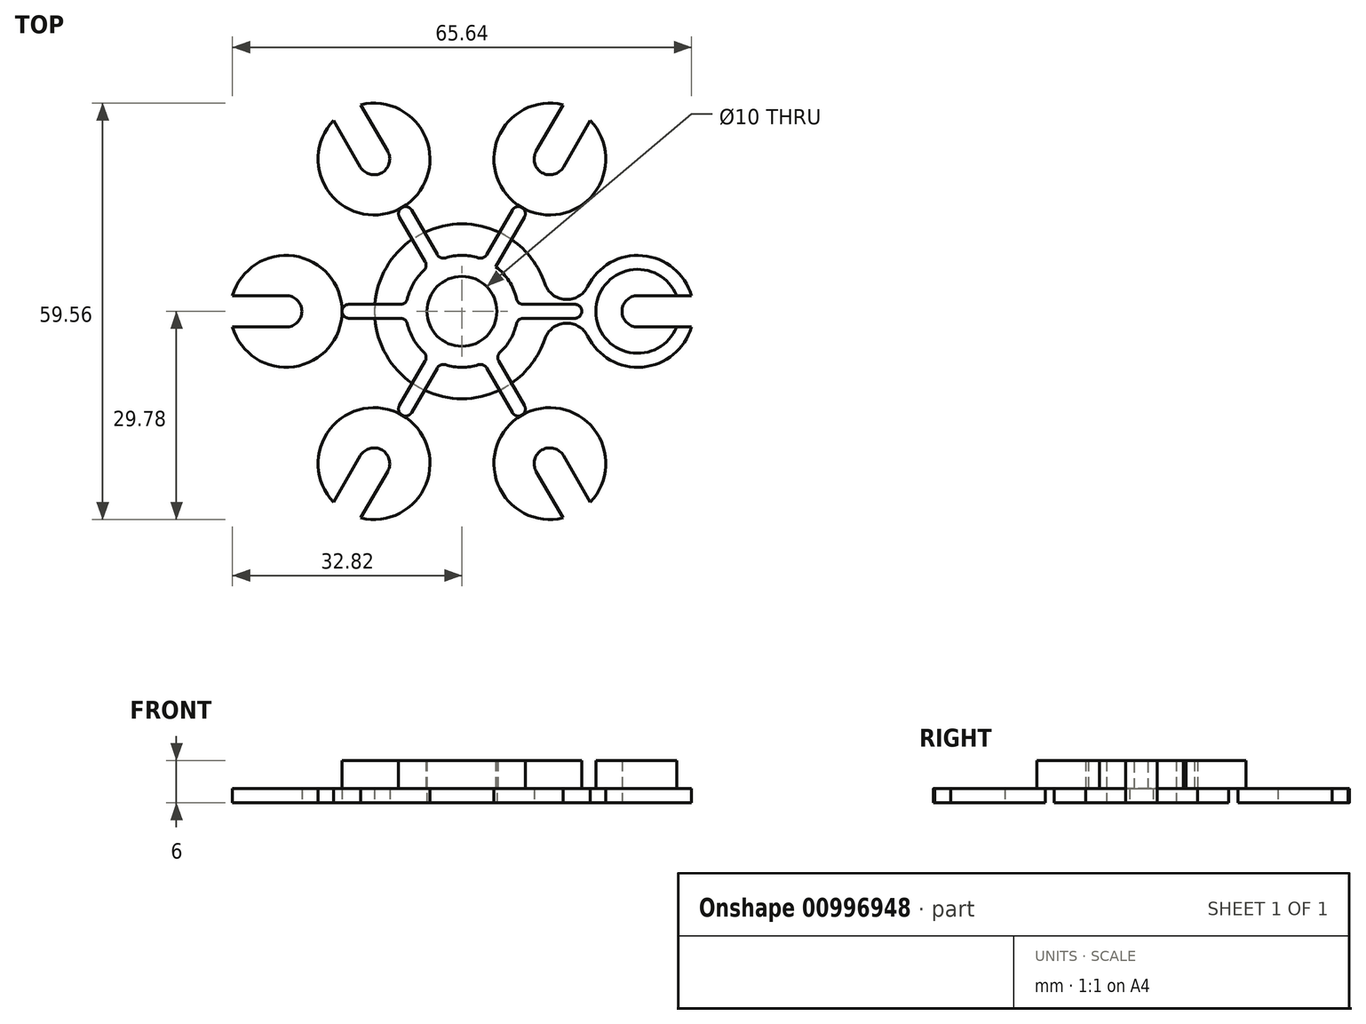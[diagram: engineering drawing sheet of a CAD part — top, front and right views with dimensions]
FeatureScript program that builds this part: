
annotation { "Feature Type Name" : "Feature", "Feature Type Description" : "" }
export const myFeature = defineFeature(function(context is Context, id is Id, definition is map)
    precondition{}
    {
        {
            var Q0;
            Q0=qCreatedBy(makeId("Top.planeOp"),FACE);
            var sketch = newSketch(context, id + "F0", { "sketchPlane" : qUnion([Q0])});
            skCircle(sketch, "E0", {"center": v(25.15, 0) * mm, "radius": 8 * mm});
            skCircle(sketch, "E1", {"center": v(0, 0) * mm, "radius": 12.5 * mm});
            skArc(sketch, "E2", {"start": v(11.86, 3.95) * mm, "mid": v(14.77, 1.7) * mm, "end": v(17.97, 3.54) * mm});
            skArc(sketch, "E3.MirrorCS", {"start": v(11.86, -3.95) * mm, "mid": v(14.77, -1.7) * mm, "end": v(17.97, -3.54) * mm});
            skCircle(sketch, "E4", {"center": v(25.15, 0) * mm, "radius": 2.25 * mm});
            skLineSegment(sketch, "E5", {"start": v(25.15, 2.25) * mm, "end": v(32.82, 2.25) * mm});
            skLineSegment(sketch, "E6.MirrorCS", {"start": v(25.15, -2.25) * mm, "end": v(32.82, -2.25) * mm});
            skCircle(sketch, "E7.1.0", {"center": v(12.57, 21.78) * mm, "radius": 2.25 * mm});
            skArc(sketch, "E7.1.1", {"start": v(9.35, 8.3) * mm, "mid": v(8.86, 11.95) * mm, "end": v(12.05, 13.8) * mm});
            skLineSegment(sketch, "E7.1.2", {"start": v(14.52, 20.65) * mm, "end": v(18.36, 27.3) * mm});
            skCircle(sketch, "E7.1.3", {"center": v(12.57, 21.78) * mm, "radius": 8 * mm});
            skLineSegment(sketch, "E7.1.4", {"start": v(10.62, 22.9) * mm, "end": v(14.46, 29.55) * mm});
            skArc(sketch, "E7.1.5", {"start": v(2.5, 12.25) * mm, "mid": v(5.92, 13.64) * mm, "end": v(5.92, 17.33) * mm});
            skCircle(sketch, "E7.2.0", {"center": v(-12.57, 21.78) * mm, "radius": 2.25 * mm});
            skArc(sketch, "E7.2.1", {"start": v(-2.5, 12.25) * mm, "mid": v(-5.92, 13.64) * mm, "end": v(-5.92, 17.33) * mm});
            skLineSegment(sketch, "E7.2.2", {"start": v(-10.62, 22.9) * mm, "end": v(-14.46, 29.55) * mm});
            skCircle(sketch, "E7.2.3", {"center": v(-12.57, 21.78) * mm, "radius": 8 * mm});
            skLineSegment(sketch, "E7.2.4", {"start": v(-14.52, 20.65) * mm, "end": v(-18.36, 27.3) * mm});
            skArc(sketch, "E7.2.5", {"start": v(-9.35, 8.3) * mm, "mid": v(-8.86, 11.95) * mm, "end": v(-12.05, 13.8) * mm});
            skCircle(sketch, "E7.3.0", {"center": v(-25.15, 0) * mm, "radius": 2.25 * mm});
            skArc(sketch, "E7.3.1", {"start": v(-11.86, 3.95) * mm, "mid": v(-14.77, 1.7) * mm, "end": v(-17.97, 3.54) * mm});
            skLineSegment(sketch, "E7.3.2", {"start": v(-25.15, 2.25) * mm, "end": v(-32.82, 2.25) * mm});
            skCircle(sketch, "E7.3.3", {"center": v(-25.15, 0) * mm, "radius": 8 * mm});
            skLineSegment(sketch, "E7.3.4", {"start": v(-25.15, -2.25) * mm, "end": v(-32.82, -2.25) * mm});
            skArc(sketch, "E7.3.5", {"start": v(-11.86, -3.95) * mm, "mid": v(-14.77, -1.7) * mm, "end": v(-17.97, -3.54) * mm});
            skCircle(sketch, "E7.4.0", {"center": v(-12.57, -21.78) * mm, "radius": 2.25 * mm});
            skArc(sketch, "E7.4.1", {"start": v(-9.35, -8.3) * mm, "mid": v(-8.86, -11.95) * mm, "end": v(-12.05, -13.8) * mm});
            skLineSegment(sketch, "E7.4.2", {"start": v(-14.52, -20.65) * mm, "end": v(-18.36, -27.3) * mm});
            skCircle(sketch, "E7.4.3", {"center": v(-12.57, -21.78) * mm, "radius": 8 * mm});
            skLineSegment(sketch, "E7.4.4", {"start": v(-10.62, -22.9) * mm, "end": v(-14.46, -29.55) * mm});
            skArc(sketch, "E7.4.5", {"start": v(-2.5, -12.25) * mm, "mid": v(-5.92, -13.64) * mm, "end": v(-5.92, -17.33) * mm});
            skCircle(sketch, "E7.5.0", {"center": v(12.57, -21.78) * mm, "radius": 2.25 * mm});
            skArc(sketch, "E7.5.1", {"start": v(2.5, -12.25) * mm, "mid": v(5.92, -13.64) * mm, "end": v(5.92, -17.33) * mm});
            skLineSegment(sketch, "E7.5.2", {"start": v(10.62, -22.9) * mm, "end": v(14.46, -29.55) * mm});
            skCircle(sketch, "E7.5.3", {"center": v(12.57, -21.78) * mm, "radius": 8 * mm});
            skLineSegment(sketch, "E7.5.4", {"start": v(14.52, -20.65) * mm, "end": v(18.36, -27.3) * mm});
            skArc(sketch, "E7.5.5", {"start": v(9.35, -8.3) * mm, "mid": v(8.86, -11.95) * mm, "end": v(12.05, -13.8) * mm});
            skCircle(sketch, "E8", {"center": v(0, 0) * mm, "radius": 5 * mm});
            skSolve(sketch);
        }
        {
            var Q0;
            {var subQ0=sQuery(id+"F0.wireOp",EDGE,"E5");Q0=makeQuery(id+"F0.imprint","IMPRINT",FACE,{"disambiguationData":[TD([[makeQuery(id+"F0.imprint","IMPRINT",EDGE,{"derivedFrom":subQ0}),1.0]])]});}
            var Q1;
            {var subQ0=sQuery(id+"F0.wireOp",EDGE,"E2");Q1=makeQuery(id+"F0.imprint","IMPRINT",FACE,{"disambiguationData":[TD([[makeQuery(id+"F0.imprint","IMPRINT",EDGE,{"derivedFrom":subQ0}),-1.0]])]});}
            var Q2;
            {var subQ0=sQuery(id+"F0.wireOp",EDGE,"E1");var subQ8=makeQuery(id+"F0.imprint","INTERSECT",VERTEX,{"derivedFrom":[subQ0,sQuery(id+"F0.wireOp",EDGE,"E2")]});Q2=makeQuery(id+"F0.imprint","IMPRINT",FACE,{"disambiguationData":[TD([[makeQuery(id+"F0.imprint","IMPRINT",EDGE,{"disambiguationData":[TD([[subQ8,-1.0]])],"derivedFrom":subQ0}),1.0]])]});}
            var Q3;
            {var subQ0=sQuery(id+"F0.wireOp",EDGE,"19b5fdfa-99aa-4df6-ab24-c400294d4a82.1.0");Q3=makeQuery(id+"F0.imprint","IMPRINT",FACE,{"disambiguationData":[TD([[makeQuery(id+"F0.imprint","IMPRINT",EDGE,{"derivedFrom":subQ0}),1.0]])]});}
            var Q4;
            {var subQ0=sQuery(id+"F0.wireOp",EDGE,"20f51366-0cb7-4326-9ac2-2f9416bb62c2.1.0");Q4=makeQuery(id+"F0.imprint","IMPRINT",FACE,{"disambiguationData":[TD([[makeQuery(id+"F0.imprint","IMPRINT",EDGE,{"derivedFrom":subQ0}),-1.0]])]});}
            var Q5;
            {var subQ0=sQuery(id+"F0.wireOp",EDGE,"20f51366-0cb7-4326-9ac2-2f9416bb62c2.2.0");Q5=makeQuery(id+"F0.imprint","IMPRINT",FACE,{"disambiguationData":[TD([[makeQuery(id+"F0.imprint","IMPRINT",EDGE,{"derivedFrom":subQ0}),-1.0]])]});}
            var Q6;
            {var subQ4=sQuery(id+"F0.wireOp",EDGE,"19b5fdfa-99aa-4df6-ab24-c400294d4a82.2.0");Q6=makeQuery(id+"F0.imprint","IMPRINT",FACE,{"disambiguationData":[TD([[makeQuery(id+"F0.imprint","IMPRINT",EDGE,{"derivedFrom":subQ4}),1.0]])]});}
            var Q7;
            {var subQ0=sQuery(id+"F0.wireOp",EDGE,"19b5fdfa-99aa-4df6-ab24-c400294d4a82.3.0");Q7=makeQuery(id+"F0.imprint","IMPRINT",FACE,{"disambiguationData":[TD([[makeQuery(id+"F0.imprint","IMPRINT",EDGE,{"derivedFrom":subQ0}),1.0]])]});}
            var Q8;
            {var subQ0=sQuery(id+"F0.wireOp",EDGE,"20f51366-0cb7-4326-9ac2-2f9416bb62c2.3.0");Q8=makeQuery(id+"F0.imprint","IMPRINT",FACE,{"disambiguationData":[TD([[makeQuery(id+"F0.imprint","IMPRINT",EDGE,{"derivedFrom":subQ0}),-1.0]])]});}
            var Q9;
            {var subQ0=sQuery(id+"F0.wireOp",EDGE,"20f51366-0cb7-4326-9ac2-2f9416bb62c2.4.0");Q9=makeQuery(id+"F0.imprint","IMPRINT",FACE,{"disambiguationData":[TD([[makeQuery(id+"F0.imprint","IMPRINT",EDGE,{"derivedFrom":subQ0}),-1.0]])]});}
            var Q10;
            {var subQ3=sQuery(id+"F0.wireOp",EDGE,"19b5fdfa-99aa-4df6-ab24-c400294d4a82.4.0");Q10=makeQuery(id+"F0.imprint","IMPRINT",FACE,{"disambiguationData":[TD([[makeQuery(id+"F0.imprint","IMPRINT",EDGE,{"derivedFrom":subQ3}),1.0]])]});}
            var Q11;
            {var subQ0=sQuery(id+"F0.wireOp",EDGE,"20f51366-0cb7-4326-9ac2-2f9416bb62c2.5.0");Q11=makeQuery(id+"F0.imprint","IMPRINT",FACE,{"disambiguationData":[TD([[makeQuery(id+"F0.imprint","IMPRINT",EDGE,{"derivedFrom":subQ0}),-1.0]])]});}
            var Q12;
            {var subQ0=sQuery(id+"F0.wireOp",EDGE,"19b5fdfa-99aa-4df6-ab24-c400294d4a82.5.0");Q12=makeQuery(id+"F0.imprint","IMPRINT",FACE,{"disambiguationData":[TD([[makeQuery(id+"F0.imprint","IMPRINT",EDGE,{"derivedFrom":subQ0}),1.0]])]});}
            var Q13;
            {var subQ0=sQuery(id+"F0.wireOp",EDGE,"E7.1.1");Q13=makeQuery(id+"F0.imprint","IMPRINT",FACE,{"disambiguationData":[TD([[makeQuery(id+"F0.imprint","IMPRINT",EDGE,{"derivedFrom":subQ0}),1.0]])]});}
            var Q14;
            {var subQ0=sQuery(id+"F0.wireOp",EDGE,"E7.2.1");Q14=makeQuery(id+"F0.imprint","IMPRINT",FACE,{"disambiguationData":[TD([[makeQuery(id+"F0.imprint","IMPRINT",EDGE,{"derivedFrom":subQ0}),1.0]])]});}
            var Q15;
            {var subQ0=sQuery(id+"F0.wireOp",EDGE,"E7.3.1");Q15=makeQuery(id+"F0.imprint","IMPRINT",FACE,{"disambiguationData":[TD([[makeQuery(id+"F0.imprint","IMPRINT",EDGE,{"derivedFrom":subQ0}),1.0]])]});}
            var Q16;
            {var subQ0=sQuery(id+"F0.wireOp",EDGE,"E7.4.1");Q16=makeQuery(id+"F0.imprint","IMPRINT",FACE,{"disambiguationData":[TD([[makeQuery(id+"F0.imprint","IMPRINT",EDGE,{"derivedFrom":subQ0}),1.0]])]});}
            var Q17;
            {var subQ0=sQuery(id+"F0.wireOp",EDGE,"E7.5.1");Q17=makeQuery(id+"F0.imprint","IMPRINT",FACE,{"disambiguationData":[TD([[makeQuery(id+"F0.imprint","IMPRINT",EDGE,{"derivedFrom":subQ0}),1.0]])]});}
            var Q18;
            {var subQ3=sQuery(id+"F0.wireOp",EDGE,"E7.5.2");Q18=makeQuery(id+"F0.imprint","IMPRINT",FACE,{"disambiguationData":[TD([[makeQuery(id+"F0.imprint","IMPRINT",EDGE,{"derivedFrom":subQ3}),-1.0]])]});}
            var Q19;
            {var subQ3=sQuery(id+"F0.wireOp",EDGE,"E7.4.2");Q19=makeQuery(id+"F0.imprint","IMPRINT",FACE,{"disambiguationData":[TD([[makeQuery(id+"F0.imprint","IMPRINT",EDGE,{"derivedFrom":subQ3}),-1.0]])]});}
            var Q20;
            {var subQ3=sQuery(id+"F0.wireOp",EDGE,"E7.3.2");Q20=makeQuery(id+"F0.imprint","IMPRINT",FACE,{"disambiguationData":[TD([[makeQuery(id+"F0.imprint","IMPRINT",EDGE,{"derivedFrom":subQ3}),-1.0]])]});}
            var Q21;
            {var subQ3=sQuery(id+"F0.wireOp",EDGE,"E7.2.2");Q21=makeQuery(id+"F0.imprint","IMPRINT",FACE,{"disambiguationData":[TD([[makeQuery(id+"F0.imprint","IMPRINT",EDGE,{"derivedFrom":subQ3}),-1.0]])]});}
            var Q22;
            {var subQ3=sQuery(id+"F0.wireOp",EDGE,"E7.1.2");Q22=makeQuery(id+"F0.imprint","IMPRINT",FACE,{"disambiguationData":[TD([[makeQuery(id+"F0.imprint","IMPRINT",EDGE,{"derivedFrom":subQ3}),-1.0]])]});}
            extrude(context, id + "F1", {"entities" : qUnion([Q0, Q1, Q2, Q3, Q4, Q5, Q6, Q7, Q8, Q9, Q10, Q11, Q12, Q13, Q14, Q15, Q16, Q17, Q18, Q19, Q20, Q21, Q22]), "depth" : 2 * mm, "offsetDistance" : 25 * mm});
        }
        {
            var Q0;
            Q0=makeQuery(id+"F1.opExtrude","CAP_FACE",FACE,{"disambiguationData":[OSD([sQuery(id+"F0.wireOp",EDGE,"E0"),sQuery(id+"F0.wireOp",EDGE,"E1"),sQuery(id+"F0.wireOp",EDGE,"E2"),sQuery(id+"F0.wireOp",EDGE,"E3.MirrorCS"),sQuery(id+"F0.wireOp",EDGE,"20f51366-0cb7-4326-9ac2-2f9416bb62c2.1.0"),sQuery(id+"F0.wireOp",EDGE,"20f51366-0cb7-4326-9ac2-2f9416bb62c2.1.1"),sQuery(id+"F0.wireOp",EDGE,"20f51366-0cb7-4326-9ac2-2f9416bb62c2.1.2"),sQuery(id+"F0.wireOp",EDGE,"20f51366-0cb7-4326-9ac2-2f9416bb62c2.2.0"),sQuery(id+"F0.wireOp",EDGE,"20f51366-0cb7-4326-9ac2-2f9416bb62c2.2.1"),sQuery(id+"F0.wireOp",EDGE,"20f51366-0cb7-4326-9ac2-2f9416bb62c2.2.2"),sQuery(id+"F0.wireOp",EDGE,"20f51366-0cb7-4326-9ac2-2f9416bb62c2.3.0"),sQuery(id+"F0.wireOp",EDGE,"20f51366-0cb7-4326-9ac2-2f9416bb62c2.3.1"),sQuery(id+"F0.wireOp",EDGE,"20f51366-0cb7-4326-9ac2-2f9416bb62c2.3.2"),sQuery(id+"F0.wireOp",EDGE,"20f51366-0cb7-4326-9ac2-2f9416bb62c2.4.0"),sQuery(id+"F0.wireOp",EDGE,"20f51366-0cb7-4326-9ac2-2f9416bb62c2.4.1"),sQuery(id+"F0.wireOp",EDGE,"20f51366-0cb7-4326-9ac2-2f9416bb62c2.4.2"),sQuery(id+"F0.wireOp",EDGE,"20f51366-0cb7-4326-9ac2-2f9416bb62c2.5.0"),sQuery(id+"F0.wireOp",EDGE,"20f51366-0cb7-4326-9ac2-2f9416bb62c2.5.1"),sQuery(id+"F0.wireOp",EDGE,"20f51366-0cb7-4326-9ac2-2f9416bb62c2.5.2"),sQuery(id+"F0.wireOp",EDGE,"E4"),sQuery(id+"F0.wireOp",EDGE,"E5"),sQuery(id+"F0.wireOp",EDGE,"E6.MirrorCS"),sQuery(id+"F0.wireOp",EDGE,"19b5fdfa-99aa-4df6-ab24-c400294d4a82.1.0"),sQuery(id+"F0.wireOp",EDGE,"19b5fdfa-99aa-4df6-ab24-c400294d4a82.1.1"),sQuery(id+"F0.wireOp",EDGE,"19b5fdfa-99aa-4df6-ab24-c400294d4a82.1.2"),sQuery(id+"F0.wireOp",EDGE,"19b5fdfa-99aa-4df6-ab24-c400294d4a82.2.0"),sQuery(id+"F0.wireOp",EDGE,"19b5fdfa-99aa-4df6-ab24-c400294d4a82.2.1"),sQuery(id+"F0.wireOp",EDGE,"19b5fdfa-99aa-4df6-ab24-c400294d4a82.2.2"),sQuery(id+"F0.wireOp",EDGE,"19b5fdfa-99aa-4df6-ab24-c400294d4a82.3.0"),sQuery(id+"F0.wireOp",EDGE,"19b5fdfa-99aa-4df6-ab24-c400294d4a82.3.1"),sQuery(id+"F0.wireOp",EDGE,"19b5fdfa-99aa-4df6-ab24-c400294d4a82.3.2"),sQuery(id+"F0.wireOp",EDGE,"19b5fdfa-99aa-4df6-ab24-c400294d4a82.4.0"),sQuery(id+"F0.wireOp",EDGE,"19b5fdfa-99aa-4df6-ab24-c400294d4a82.4.1"),sQuery(id+"F0.wireOp",EDGE,"19b5fdfa-99aa-4df6-ab24-c400294d4a82.4.2"),sQuery(id+"F0.wireOp",EDGE,"19b5fdfa-99aa-4df6-ab24-c400294d4a82.5.0"),sQuery(id+"F0.wireOp",EDGE,"19b5fdfa-99aa-4df6-ab24-c400294d4a82.5.1"),sQuery(id+"F0.wireOp",EDGE,"19b5fdfa-99aa-4df6-ab24-c400294d4a82.5.2"),sQuery(id+"F0.wireOp",EDGE,"Dy7Ucuv2-wQet-6OGx-sShq-DWIG0Ccbs11O")])],"isStart":false});
            var sketch = newSketch(context, id + "F2", { "sketchPlane" : qUnion([Q0])});
            skArc(sketch, "E9", {"start": v(32.82, -2.25) * mm, "mid": v(17.15, 0) * mm, "end": v(32.82, 2.25) * mm});
            skArc(sketch, "E10", {"start": v(30.7, -2.25) * mm, "mid": v(19.15, 0) * mm, "end": v(30.7, 2.25) * mm});
            skCircle(sketch, "E11", {"center": v(0, 0) * mm, "radius": 8 * mm});
            skLineSegment(sketch, "E12", {"start": v(17.2, 1) * mm, "end": v(7.94, 1) * mm});
            skLineSegment(sketch, "E13.MirrorCS", {"start": v(17.2, -1) * mm, "end": v(7.94, -1) * mm});
            skLineSegment(sketch, "E14.1.0", {"start": v(7.74, 15.4) * mm, "end": v(3.1, 7.37) * mm});
            skLineSegment(sketch, "E14.1.1", {"start": v(9.47, 14.4) * mm, "end": v(4.83, 6.37) * mm});
            skArc(sketch, "E14.1.2", {"start": v(18.36, 27.3) * mm, "mid": v(8.57, 14.85) * mm, "end": v(14.46, 29.55) * mm});
            skArc(sketch, "E14.1.3", {"start": v(17.3, 25.47) * mm, "mid": v(9.57, 16.58) * mm, "end": v(13.4, 27.72) * mm});
            skLineSegment(sketch, "E14.2.0", {"start": v(-9.47, 14.4) * mm, "end": v(-4.83, 6.37) * mm});
            skLineSegment(sketch, "E14.2.1", {"start": v(-7.74, 15.4) * mm, "end": v(-3.1, 7.37) * mm});
            skArc(sketch, "E14.2.2", {"start": v(-14.46, 29.55) * mm, "mid": v(-8.57, 14.85) * mm, "end": v(-18.36, 27.3) * mm});
            skArc(sketch, "E14.2.3", {"start": v(-13.4, 27.72) * mm, "mid": v(-9.57, 16.58) * mm, "end": v(-17.3, 25.47) * mm});
            skLineSegment(sketch, "E14.3.0", {"start": v(-17.2, -1) * mm, "end": v(-7.94, -1) * mm});
            skLineSegment(sketch, "E14.3.1", {"start": v(-17.2, 1) * mm, "end": v(-7.94, 1) * mm});
            skArc(sketch, "E14.3.2", {"start": v(-32.82, 2.25) * mm, "mid": v(-17.15, 0) * mm, "end": v(-32.82, -2.25) * mm});
            skArc(sketch, "E14.3.3", {"start": v(-30.7, 2.25) * mm, "mid": v(-19.15, 0) * mm, "end": v(-30.7, -2.25) * mm});
            skLineSegment(sketch, "E14.4.0", {"start": v(-7.74, -15.4) * mm, "end": v(-3.1, -7.37) * mm});
            skLineSegment(sketch, "E14.4.1", {"start": v(-9.47, -14.4) * mm, "end": v(-4.83, -6.37) * mm});
            skArc(sketch, "E14.4.2", {"start": v(-18.36, -27.3) * mm, "mid": v(-8.57, -14.85) * mm, "end": v(-14.46, -29.55) * mm});
            skArc(sketch, "E14.4.3", {"start": v(-17.3, -25.47) * mm, "mid": v(-9.57, -16.58) * mm, "end": v(-13.4, -27.72) * mm});
            skLineSegment(sketch, "E14.5.0", {"start": v(9.47, -14.4) * mm, "end": v(4.83, -6.37) * mm});
            skLineSegment(sketch, "E14.5.1", {"start": v(7.74, -15.4) * mm, "end": v(3.1, -7.37) * mm});
            skArc(sketch, "E14.5.2", {"start": v(14.46, -29.55) * mm, "mid": v(8.57, -14.85) * mm, "end": v(18.36, -27.3) * mm});
            skArc(sketch, "E14.5.3", {"start": v(13.4, -27.72) * mm, "mid": v(9.57, -16.58) * mm, "end": v(17.3, -25.47) * mm});
            skSolve(sketch);
        }
        {
            var Q0;
            {var subQ0=sQuery(id+"F2.wireOp",EDGE,"E12");Q0=makeQuery(id+"F2.imprint","IMPRINT",FACE,{"disambiguationData":[TD([[makeQuery(id+"F2.imprint","IMPRINT",EDGE,{"derivedFrom":subQ0}),1.0]])]});}
            var Q1;
            {var subQ9=sQuery(id+"F2.wireOp",EDGE,"E10");Q1=makeQuery(id+"F2.imprint","IMPRINT",FACE,{"disambiguationData":[TD([[makeQuery(id+"F2.imprint","IMPRINT",EDGE,{"derivedFrom":subQ9}),1.0]])]});}
            var Q2;
            Q2=makeQuery(id+"F2.imprint","IMPRINT",FACE,{"disambiguationData":[TD([[makeQuery(id+"F2.imprint","IMPRINT",EDGE,{"derivedFrom":makeQuery(id+"F1.opExtrude","CAP_EDGE",EDGE,{"disambiguationData":[OSD([sQuery(id+"F0.wireOp",EDGE,"E8")])],"isStart":false})}),-1.0]])]});
            var Q3;
            {var subQ0=sQuery(id+"F2.wireOp",EDGE,"E14.5.0");Q3=makeQuery(id+"F2.imprint","IMPRINT",FACE,{"disambiguationData":[TD([[makeQuery(id+"F2.imprint","IMPRINT",EDGE,{"derivedFrom":subQ0}),1.0]])]});}
            var Q4;
            {var subQ9=sQuery(id+"F2.wireOp",EDGE,"E14.5.3");Q4=makeQuery(id+"F2.imprint","IMPRINT",FACE,{"disambiguationData":[TD([[makeQuery(id+"F2.imprint","IMPRINT",EDGE,{"derivedFrom":subQ9}),1.0]])]});}
            var Q5;
            {var subQ5=sQuery(id+"F2.wireOp",EDGE,"E14.4.3");Q5=makeQuery(id+"F2.imprint","IMPRINT",FACE,{"disambiguationData":[TD([[makeQuery(id+"F2.imprint","IMPRINT",EDGE,{"derivedFrom":subQ5}),1.0]])]});}
            var Q6;
            {var subQ0=sQuery(id+"F2.wireOp",EDGE,"E14.4.0");Q6=makeQuery(id+"F2.imprint","IMPRINT",FACE,{"disambiguationData":[TD([[makeQuery(id+"F2.imprint","IMPRINT",EDGE,{"derivedFrom":subQ0}),1.0]])]});}
            var Q7;
            {var subQ0=sQuery(id+"F2.wireOp",EDGE,"E14.3.0");Q7=makeQuery(id+"F2.imprint","IMPRINT",FACE,{"disambiguationData":[TD([[makeQuery(id+"F2.imprint","IMPRINT",EDGE,{"derivedFrom":subQ0}),1.0]])]});}
            var Q8;
            {var subQ9=sQuery(id+"F2.wireOp",EDGE,"E14.3.3");Q8=makeQuery(id+"F2.imprint","IMPRINT",FACE,{"disambiguationData":[TD([[makeQuery(id+"F2.imprint","IMPRINT",EDGE,{"derivedFrom":subQ9}),1.0]])]});}
            var Q9;
            {var subQ7=sQuery(id+"F2.wireOp",EDGE,"E14.2.3");Q9=makeQuery(id+"F2.imprint","IMPRINT",FACE,{"disambiguationData":[TD([[makeQuery(id+"F2.imprint","IMPRINT",EDGE,{"derivedFrom":subQ7}),1.0]])]});}
            var Q10;
            {var subQ0=sQuery(id+"F2.wireOp",EDGE,"E14.2.0");Q10=makeQuery(id+"F2.imprint","IMPRINT",FACE,{"disambiguationData":[TD([[makeQuery(id+"F2.imprint","IMPRINT",EDGE,{"derivedFrom":subQ0}),1.0]])]});}
            var Q11;
            {var subQ0=sQuery(id+"F2.wireOp",EDGE,"E14.1.0");Q11=makeQuery(id+"F2.imprint","IMPRINT",FACE,{"disambiguationData":[TD([[makeQuery(id+"F2.imprint","IMPRINT",EDGE,{"derivedFrom":subQ0}),1.0]])]});}
            var Q12;
            {var subQ6=sQuery(id+"F2.wireOp",EDGE,"E14.1.3");Q12=makeQuery(id+"F2.imprint","IMPRINT",FACE,{"disambiguationData":[TD([[makeQuery(id+"F2.imprint","IMPRINT",EDGE,{"derivedFrom":subQ6}),1.0]])]});}
            extrude(context, id + "F3", {"entities" : qUnion([Q0, Q1, Q2, Q3, Q4, Q5, Q6, Q7, Q8, Q9, Q10, Q11, Q12]), "operationType" : NewBodyOperationType.ADD, "depth" : 4 * mm, "offsetDistance" : 25 * mm});
        }
        {
            var Q0;
            {var subQ0=sQuery(id+"F0.wireOp",EDGE,"E5");Q0=makeQuery(id+"F3.boolean.opBoolean","MERGE",EDGE,{"derivedFrom":[makeQuery(id+"F1.opExtrude","SWEPT_EDGE",EDGE,{"disambiguationData":[OSD([sQuery(id+"F0.wireOp",EDGE,"E0"),subQ0])]}),makeQuery(id+"F3.opExtrude","SWEPT_EDGE",EDGE,{"disambiguationData":[OSD([subQ0,sQuery(id+"F2.wireOp",EDGE,"E9")])]})]});}
            var Q1;
            {var subQ0=sQuery(id+"F0.wireOp",EDGE,"E6.MirrorCS");Q1=makeQuery(id+"F3.boolean.opBoolean","MERGE",EDGE,{"derivedFrom":[makeQuery(id+"F1.opExtrude","SWEPT_EDGE",EDGE,{"disambiguationData":[OSD([sQuery(id+"F0.wireOp",EDGE,"E0"),subQ0])]}),makeQuery(id+"F3.opExtrude","SWEPT_EDGE",EDGE,{"disambiguationData":[OSD([subQ0,sQuery(id+"F2.wireOp",EDGE,"E9")])]})]});}
            var Q2;
            {var subQ0=sQuery(id+"F0.wireOp",EDGE,"E7.1.4");Q2=makeQuery(id+"F3.boolean.opBoolean","MERGE",EDGE,{"derivedFrom":[makeQuery(id+"F1.opExtrude","SWEPT_EDGE",EDGE,{"disambiguationData":[OSD([sQuery(id+"F0.wireOp",EDGE,"E7.1.3"),subQ0])]}),makeQuery(id+"F3.opExtrude","SWEPT_EDGE",EDGE,{"disambiguationData":[OSD([subQ0,sQuery(id+"F2.wireOp",EDGE,"E14.1.2")])]})]});}
            var Q3;
            {var subQ0=sQuery(id+"F0.wireOp",EDGE,"E7.2.4");Q3=makeQuery(id+"F3.boolean.opBoolean","MERGE",EDGE,{"derivedFrom":[makeQuery(id+"F1.opExtrude","SWEPT_EDGE",EDGE,{"disambiguationData":[OSD([sQuery(id+"F0.wireOp",EDGE,"E7.2.3"),subQ0])]}),makeQuery(id+"F3.opExtrude","SWEPT_EDGE",EDGE,{"disambiguationData":[OSD([subQ0,sQuery(id+"F2.wireOp",EDGE,"E14.2.2")])]})]});}
            var Q4;
            {var subQ0=sQuery(id+"F0.wireOp",EDGE,"E7.1.2");Q4=makeQuery(id+"F3.boolean.opBoolean","MERGE",EDGE,{"derivedFrom":[makeQuery(id+"F1.opExtrude","SWEPT_EDGE",EDGE,{"disambiguationData":[OSD([subQ0,sQuery(id+"F0.wireOp",EDGE,"E7.1.3")])]}),makeQuery(id+"F3.opExtrude","SWEPT_EDGE",EDGE,{"disambiguationData":[OSD([subQ0,sQuery(id+"F2.wireOp",EDGE,"E14.1.2")])]})]});}
            var Q5;
            {var subQ0=sQuery(id+"F0.wireOp",EDGE,"E7.2.2");Q5=makeQuery(id+"F3.boolean.opBoolean","MERGE",EDGE,{"derivedFrom":[makeQuery(id+"F1.opExtrude","SWEPT_EDGE",EDGE,{"disambiguationData":[OSD([subQ0,sQuery(id+"F0.wireOp",EDGE,"E7.2.3")])]}),makeQuery(id+"F3.opExtrude","SWEPT_EDGE",EDGE,{"disambiguationData":[OSD([subQ0,sQuery(id+"F2.wireOp",EDGE,"E14.2.2")])]})]});}
            var Q6;
            {var subQ0=sQuery(id+"F0.wireOp",EDGE,"E7.3.2");Q6=makeQuery(id+"F3.boolean.opBoolean","MERGE",EDGE,{"derivedFrom":[makeQuery(id+"F1.opExtrude","SWEPT_EDGE",EDGE,{"disambiguationData":[OSD([subQ0,sQuery(id+"F0.wireOp",EDGE,"E7.3.3")])]}),makeQuery(id+"F3.opExtrude","SWEPT_EDGE",EDGE,{"disambiguationData":[OSD([subQ0,sQuery(id+"F2.wireOp",EDGE,"E14.3.2")])]})]});}
            var Q7;
            {var subQ0=sQuery(id+"F0.wireOp",EDGE,"E7.3.4");Q7=makeQuery(id+"F3.boolean.opBoolean","MERGE",EDGE,{"derivedFrom":[makeQuery(id+"F1.opExtrude","SWEPT_EDGE",EDGE,{"disambiguationData":[OSD([sQuery(id+"F0.wireOp",EDGE,"E7.3.3"),subQ0])]}),makeQuery(id+"F3.opExtrude","SWEPT_EDGE",EDGE,{"disambiguationData":[OSD([subQ0,sQuery(id+"F2.wireOp",EDGE,"E14.3.2")])]})]});}
            var Q8;
            {var subQ0=sQuery(id+"F0.wireOp",EDGE,"E7.4.2");Q8=makeQuery(id+"F3.boolean.opBoolean","MERGE",EDGE,{"derivedFrom":[makeQuery(id+"F1.opExtrude","SWEPT_EDGE",EDGE,{"disambiguationData":[OSD([subQ0,sQuery(id+"F0.wireOp",EDGE,"E7.4.3")])]}),makeQuery(id+"F3.opExtrude","SWEPT_EDGE",EDGE,{"disambiguationData":[OSD([subQ0,sQuery(id+"F2.wireOp",EDGE,"E14.4.2")])]})]});}
            var Q9;
            {var subQ0=sQuery(id+"F0.wireOp",EDGE,"E7.4.4");Q9=makeQuery(id+"F3.boolean.opBoolean","MERGE",EDGE,{"derivedFrom":[makeQuery(id+"F1.opExtrude","SWEPT_EDGE",EDGE,{"disambiguationData":[OSD([sQuery(id+"F0.wireOp",EDGE,"E7.4.3"),subQ0])]}),makeQuery(id+"F3.opExtrude","SWEPT_EDGE",EDGE,{"disambiguationData":[OSD([subQ0,sQuery(id+"F2.wireOp",EDGE,"E14.4.2")])]})]});}
            var Q10;
            {var subQ0=sQuery(id+"F0.wireOp",EDGE,"E7.5.2");Q10=makeQuery(id+"F3.boolean.opBoolean","MERGE",EDGE,{"derivedFrom":[makeQuery(id+"F1.opExtrude","SWEPT_EDGE",EDGE,{"disambiguationData":[OSD([subQ0,sQuery(id+"F0.wireOp",EDGE,"E7.5.3")])]}),makeQuery(id+"F3.opExtrude","SWEPT_EDGE",EDGE,{"disambiguationData":[OSD([subQ0,sQuery(id+"F2.wireOp",EDGE,"E14.5.2")])]})]});}
            var Q11;
            {var subQ0=sQuery(id+"F0.wireOp",EDGE,"E7.5.4");Q11=makeQuery(id+"F3.boolean.opBoolean","MERGE",EDGE,{"derivedFrom":[makeQuery(id+"F1.opExtrude","SWEPT_EDGE",EDGE,{"disambiguationData":[OSD([sQuery(id+"F0.wireOp",EDGE,"E7.5.3"),subQ0])]}),makeQuery(id+"F3.opExtrude","SWEPT_EDGE",EDGE,{"disambiguationData":[OSD([subQ0,sQuery(id+"F2.wireOp",EDGE,"E14.5.2")])]})]});}
            var Q12;
            Q12=makeQuery(id+"F3.opExtrude","SWEPT_EDGE",EDGE,{"disambiguationData":[OSD([sQuery(id+"F2.wireOp",EDGE,"E11"),sQuery(id+"F2.wireOp",EDGE,"E14.5.0")])]});
            var Q13;
            Q13=makeQuery(id+"F3.opExtrude","SWEPT_EDGE",EDGE,{"disambiguationData":[OSD([sQuery(id+"F2.wireOp",EDGE,"E14.4.0"),sQuery(id+"F2.wireOp",EDGE,"E14.4.2")])]});
            var Q14;
            Q14=makeQuery(id+"F3.opExtrude","SWEPT_EDGE",EDGE,{"disambiguationData":[OSD([sQuery(id+"F2.wireOp",EDGE,"E14.3.0"),sQuery(id+"F2.wireOp",EDGE,"E14.3.2")])]});
            var Q15;
            Q15=makeQuery(id+"F3.opExtrude","SWEPT_EDGE",EDGE,{"disambiguationData":[OSD([sQuery(id+"F2.wireOp",EDGE,"E11"),sQuery(id+"F2.wireOp",EDGE,"E14.3.1")])]});
            var Q16;
            Q16=makeQuery(id+"F3.opExtrude","SWEPT_EDGE",EDGE,{"disambiguationData":[OSD([sQuery(id+"F2.wireOp",EDGE,"E11"),sQuery(id+"F2.wireOp",EDGE,"E14.1.0")])]});
            var Q17;
            Q17=makeQuery(id+"F3.opExtrude","SWEPT_EDGE",EDGE,{"disambiguationData":[OSD([sQuery(id+"F2.wireOp",EDGE,"E9"),sQuery(id+"F2.wireOp",EDGE,"E12")])]});
            var Q18;
            Q18=makeQuery(id+"F3.opExtrude","SWEPT_EDGE",EDGE,{"disambiguationData":[OSD([sQuery(id+"F2.wireOp",EDGE,"E14.4.1"),sQuery(id+"F2.wireOp",EDGE,"E14.4.2")])]});
            var Q19;
            Q19=makeQuery(id+"F3.opExtrude","SWEPT_EDGE",EDGE,{"disambiguationData":[OSD([sQuery(id+"F2.wireOp",EDGE,"E14.3.1"),sQuery(id+"F2.wireOp",EDGE,"E14.3.2")])]});
            var Q20;
            Q20=makeQuery(id+"F3.opExtrude","SWEPT_EDGE",EDGE,{"disambiguationData":[OSD([sQuery(id+"F2.wireOp",EDGE,"E14.2.0"),sQuery(id+"F2.wireOp",EDGE,"E14.2.2")])]});
            var Q21;
            Q21=makeQuery(id+"F3.opExtrude","SWEPT_EDGE",EDGE,{"disambiguationData":[OSD([sQuery(id+"F2.wireOp",EDGE,"E14.2.1"),sQuery(id+"F2.wireOp",EDGE,"E14.2.2")])]});
            var Q22;
            Q22=makeQuery(id+"F3.opExtrude","SWEPT_EDGE",EDGE,{"disambiguationData":[OSD([sQuery(id+"F2.wireOp",EDGE,"E11"),sQuery(id+"F2.wireOp",EDGE,"E14.2.1")])]});
            var Q23;
            Q23=makeQuery(id+"F3.opExtrude","SWEPT_EDGE",EDGE,{"disambiguationData":[OSD([sQuery(id+"F2.wireOp",EDGE,"E11"),sQuery(id+"F2.wireOp",EDGE,"E12")])]});
            var Q24;
            Q24=makeQuery(id+"F3.opExtrude","SWEPT_EDGE",EDGE,{"disambiguationData":[OSD([sQuery(id+"F2.wireOp",EDGE,"E14.5.0"),sQuery(id+"F2.wireOp",EDGE,"E14.5.2")])]});
            var Q25;
            Q25=makeQuery(id+"F3.opExtrude","SWEPT_EDGE",EDGE,{"disambiguationData":[OSD([sQuery(id+"F2.wireOp",EDGE,"E9"),sQuery(id+"F2.wireOp",EDGE,"E13.MirrorCS")])]});
            var Q26;
            Q26=makeQuery(id+"F3.opExtrude","SWEPT_EDGE",EDGE,{"disambiguationData":[OSD([sQuery(id+"F2.wireOp",EDGE,"E14.5.1"),sQuery(id+"F2.wireOp",EDGE,"E14.5.2")])]});
            var Q27;
            Q27=makeQuery(id+"F3.opExtrude","SWEPT_EDGE",EDGE,{"disambiguationData":[OSD([sQuery(id+"F2.wireOp",EDGE,"E11"),sQuery(id+"F2.wireOp",EDGE,"E14.4.1")])]});
            var Q28;
            Q28=makeQuery(id+"F3.opExtrude","SWEPT_EDGE",EDGE,{"disambiguationData":[OSD([sQuery(id+"F2.wireOp",EDGE,"E11"),sQuery(id+"F2.wireOp",EDGE,"E14.4.0")])]});
            var Q29;
            Q29=makeQuery(id+"F3.opExtrude","SWEPT_EDGE",EDGE,{"disambiguationData":[OSD([sQuery(id+"F2.wireOp",EDGE,"E11"),sQuery(id+"F2.wireOp",EDGE,"E14.2.0")])]});
            var Q30;
            Q30=makeQuery(id+"F3.opExtrude","SWEPT_EDGE",EDGE,{"disambiguationData":[OSD([sQuery(id+"F2.wireOp",EDGE,"E14.1.0"),sQuery(id+"F2.wireOp",EDGE,"E14.1.2")])]});
            var Q31;
            Q31=makeQuery(id+"F3.opExtrude","SWEPT_EDGE",EDGE,{"disambiguationData":[OSD([sQuery(id+"F2.wireOp",EDGE,"E14.1.1"),sQuery(id+"F2.wireOp",EDGE,"E14.1.2")])]});
            var Q32;
            Q32=makeQuery(id+"F3.opExtrude","SWEPT_EDGE",EDGE,{"disambiguationData":[OSD([sQuery(id+"F2.wireOp",EDGE,"E11"),sQuery(id+"F2.wireOp",EDGE,"E14.5.1")])]});
            var Q33;
            Q33=makeQuery(id+"F3.opExtrude","SWEPT_EDGE",EDGE,{"disambiguationData":[OSD([sQuery(id+"F2.wireOp",EDGE,"E11"),sQuery(id+"F2.wireOp",EDGE,"E13.MirrorCS")])]});
            var Q34;
            Q34=makeQuery(id+"F3.opExtrude","SWEPT_EDGE",EDGE,{"disambiguationData":[OSD([sQuery(id+"F2.wireOp",EDGE,"E11"),sQuery(id+"F2.wireOp",EDGE,"E14.3.0")])]});
            var Q35;
            {var subQ0=sQuery(id+"F2.wireOp",EDGE,"E11");Q35=makeQuery(id+"F3.opExtrude","CAP_EDGE",EDGE,{"disambiguationData":[OSD([subQ0]),TDD([makeQuery(id+"F2.imprint","IMPRINT",EDGE,{"disambiguationData":[TD([[makeQuery(id+"F2.imprint","INTERSECT",VERTEX,{"derivedFrom":[subQ0,sQuery(id+"F2.wireOp",EDGE,"E12")]}),-1.0]])],"derivedFrom":subQ0})])],"isStart":true});}
            var Q36;
            {var subQ0=sQuery(id+"F2.wireOp",EDGE,"E11");Q36=makeQuery(id+"F3.opExtrude","CAP_EDGE",EDGE,{"disambiguationData":[OSD([subQ0]),TDD([makeQuery(id+"F2.imprint","IMPRINT",EDGE,{"disambiguationData":[TD([[makeQuery(id+"F2.imprint","INTERSECT",VERTEX,{"derivedFrom":[subQ0,sQuery(id+"F2.wireOp",EDGE,"E14.1.0")]}),-1.0]])],"derivedFrom":subQ0})])],"isStart":true});}
            var Q37;
            {var subQ0=sQuery(id+"F2.wireOp",EDGE,"E11");Q37=makeQuery(id+"F3.opExtrude","CAP_EDGE",EDGE,{"disambiguationData":[OSD([subQ0]),TDD([makeQuery(id+"F2.imprint","IMPRINT",EDGE,{"disambiguationData":[TD([[makeQuery(id+"F2.imprint","INTERSECT",VERTEX,{"derivedFrom":[subQ0,sQuery(id+"F2.wireOp",EDGE,"E14.2.0")]}),-1.0]])],"derivedFrom":subQ0})])],"isStart":true});}
            var Q38;
            {var subQ0=sQuery(id+"F2.wireOp",EDGE,"E11");Q38=makeQuery(id+"F3.opExtrude","CAP_EDGE",EDGE,{"disambiguationData":[OSD([subQ0]),TDD([makeQuery(id+"F2.imprint","IMPRINT",EDGE,{"disambiguationData":[TD([[makeQuery(id+"F2.imprint","INTERSECT",VERTEX,{"derivedFrom":[subQ0,sQuery(id+"F2.wireOp",EDGE,"E14.3.0")]}),-1.0]])],"derivedFrom":subQ0})])],"isStart":true});}
            var Q39;
            {var subQ0=sQuery(id+"F2.wireOp",EDGE,"E11");Q39=makeQuery(id+"F3.opExtrude","CAP_EDGE",EDGE,{"disambiguationData":[OSD([subQ0]),TDD([makeQuery(id+"F2.imprint","IMPRINT",EDGE,{"disambiguationData":[TD([[makeQuery(id+"F2.imprint","INTERSECT",VERTEX,{"derivedFrom":[subQ0,sQuery(id+"F2.wireOp",EDGE,"E14.4.0")]}),-1.0]])],"derivedFrom":subQ0})])],"isStart":true});}
            var Q40;
            {var subQ0=sQuery(id+"F2.wireOp",EDGE,"E11");Q40=makeQuery(id+"F3.opExtrude","CAP_EDGE",EDGE,{"disambiguationData":[OSD([subQ0]),TDD([makeQuery(id+"F2.imprint","IMPRINT",EDGE,{"disambiguationData":[TD([[makeQuery(id+"F2.imprint","INTERSECT",VERTEX,{"derivedFrom":[subQ0,sQuery(id+"F2.wireOp",EDGE,"E13.MirrorCS")]}),1.0]])],"derivedFrom":subQ0})])],"isStart":true});}
            fillet(context, id + "F4", {"entities" : qUnion([Q0, Q1, Q2, Q3, Q4, Q5, Q6, Q7, Q8, Q9, Q10, Q11, Q12, Q13, Q14, Q15, Q16, Q17, Q18, Q19, Q20, Q21, Q22, Q23, Q24, Q25, Q26, Q27, Q28, Q29, Q30, Q31, Q32, Q33, Q34, Q35, Q36, Q37, Q38, Q39, Q40]), "radius" : 1 * mm, "tangentPropagation" : true, "allowEdgeOverflow" : false});
        }
    });
